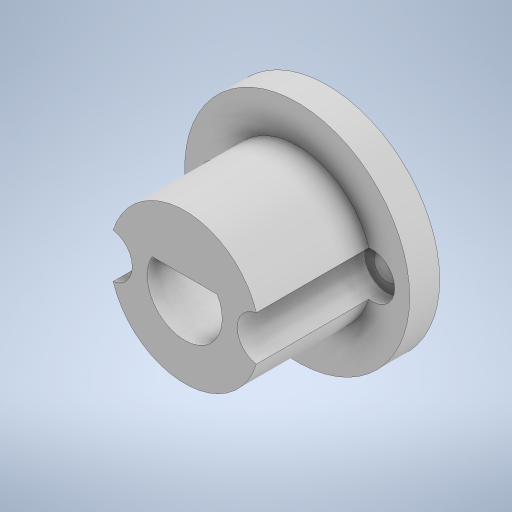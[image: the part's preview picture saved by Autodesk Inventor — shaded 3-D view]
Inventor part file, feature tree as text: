
AUTODESK INVENTOR PART (.ipt)
format: ipt  version: 2023 (Build 270158000, 158)  size: 273,920 bytes
history: native  units: in
note: dims shown in document units (in); Inventor stores cm internally (conversion verified against a paired STEP export)
features: sketch x3, extrude x2, hole x1
ambient origin geometry x8: Origin, YZ Plane, XZ Plane, XY Plane, X Axis, Y Axis, Z Axis, Center Point
bodies: Solid1 (feature_tree)
feature tree (6):
  extrude  "Extrusion1"  Depth=0.1575in TaperAngle=0.0deg
  hole  "Hole1"  [1 undecoded]
  extrude  "Extrusion2"  Depth=0.5906in
  sketch  "Sketch1"  dims[d0=1.1811in d1=0.1575in d2=0.0in]
  sketch  "Sketch2"  dims[d3=0.1378in d4=0.2362in d5=0.2362in d6=0.0787in d7=90.0deg d8=0.2362in d9=0.0in d10=0.7874in]
  sketch  "Sketch4"  dims[d12=0.3937in d13=0.0984in d14=0.3937in d15=0.3937in d16=0.5906in d17=0.0in]
note: 1 required parameter value undecoded (feature->parameter linkage not recoverable at this tier; creation-order binding heuristic only, values carry confidence <= 0.55)
